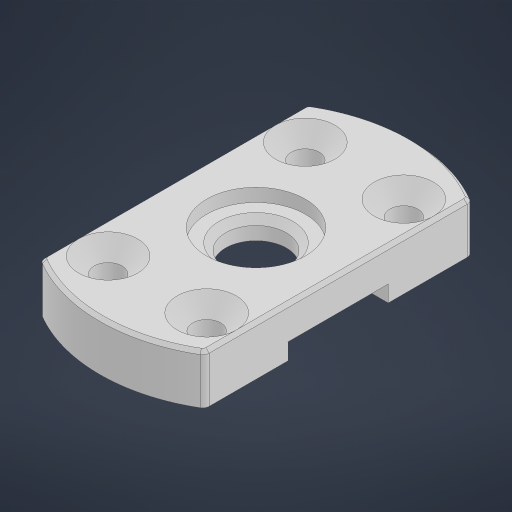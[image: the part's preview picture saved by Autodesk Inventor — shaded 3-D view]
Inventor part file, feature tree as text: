
AUTODESK INVENTOR PART (.ipt)
format: ipt  version: 2024.3 (Build 283343000, 343)  size: 245,760 bytes
history: native  units: mm
features: extrude x4, sketch x4, chamfer x2, hole x1, fillet x1, projected_geometry x1
ambient origin geometry x8: Origin, YZ Plane, XZ Plane, XY Plane, X Axis, Y Axis, Z Axis, Center Point
bodies: Body1 (feature_tree)
feature tree (13):
  extrude  "Extrusion2"  Depth=50.0mm
  sketch  "Sketch3"  dims[d5=15.0mm d6=0.0mm d7=30.5mm]
  extrude  "Extrusion3"  Depth=30.5mm
  extrude  "Extrusion4"  Depth=5.0mm
  extrude  "Extrusion5"  Depth=2.0mm
  chamfer  "Chamfer1"  Distance=4.0mm
  hole  "Hole1"  [1 undecoded]
  fillet  "Fillet1"  Radius=30.0mm
  chamfer  "Chamfer2"  Distance=60.0mm
  sketch  "Sketch2"  dims[d3=95.0mm d4=50.0mm]
  projected_geometry  "Projected Loop1"
  sketch  "Sketch4"  dims[d8=5.0mm d9=0.0mm d10=18.5mm]
  sketch  "Sketch5"  dims[d11=0.0mm d12=0.0mm d13=30.0mm d14=4.0mm d15=0.0mm d16=2.0mm d17=2.0mm d18=45.0deg d19=30.0mm d20=60.0mm d21=8.5mm d22=16.0mm d23=18.0mm d24=2.0mm d25=90.0deg d26=20.4mm d27=20.594885mm d28=1.0mm d29=2.0mm d30=45.0deg d31=2.0mm]
note: 1 required parameter value undecoded (feature->parameter linkage not recoverable at this tier; creation-order binding heuristic only, values carry confidence <= 0.55)
